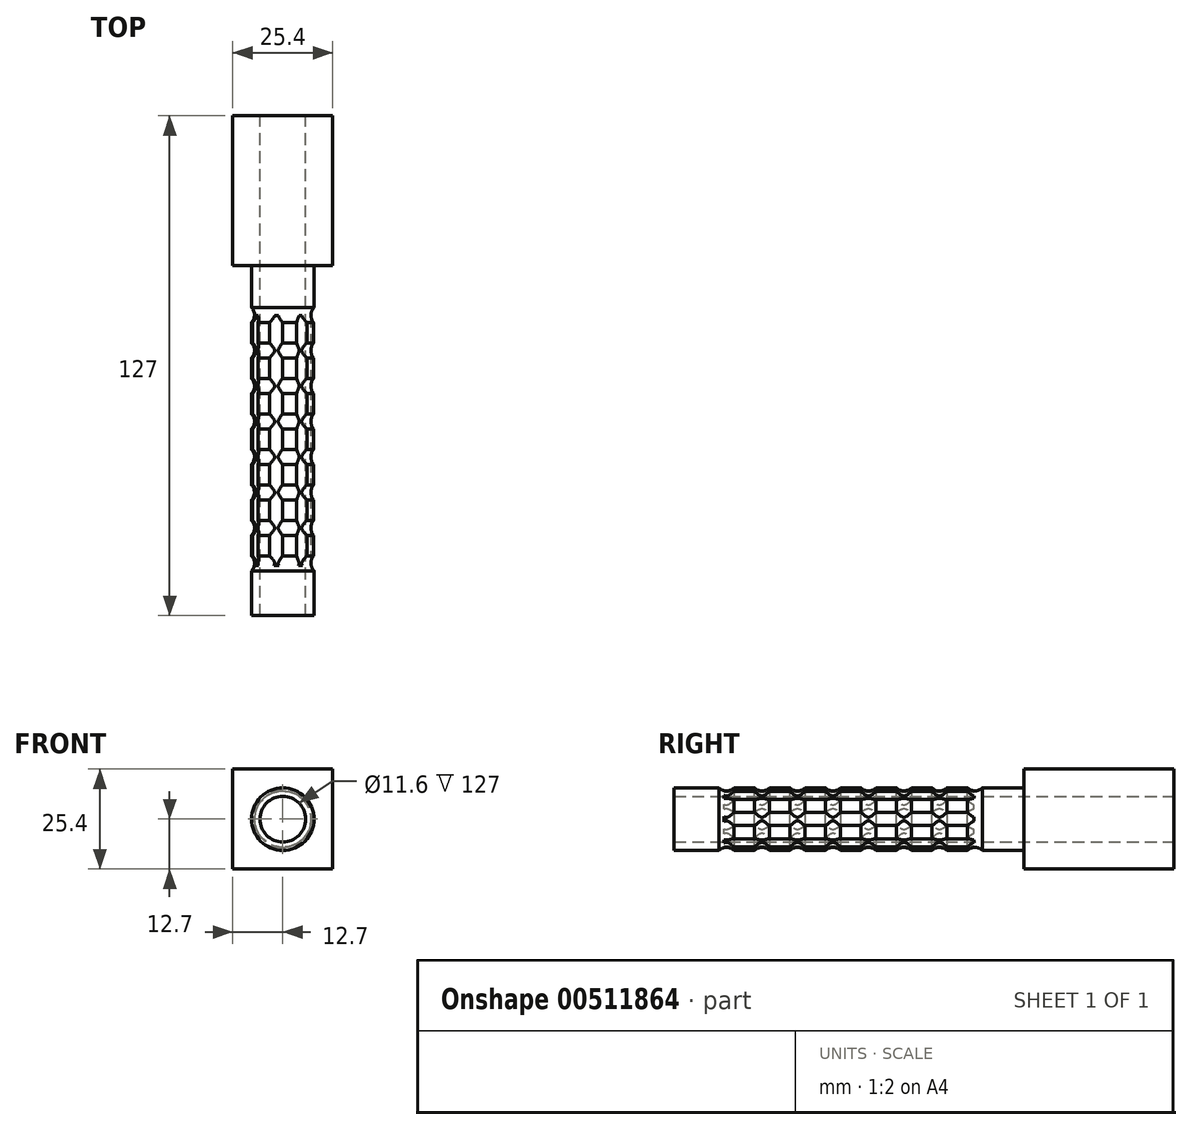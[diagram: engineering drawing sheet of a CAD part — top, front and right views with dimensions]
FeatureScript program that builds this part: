
annotation { "Feature Type Name" : "Feature", "Feature Type Description" : "" }
export const myFeature = defineFeature(function(context is Context, id is Id, definition is map)
    precondition{}
    {
        {
            var Q0;
            Q0=qCreatedBy(makeId("Front.planeOp"),FACE);
            var sketch = newSketch(context, id + "F0", { "sketchPlane" : qUnion([Q0])});
            skLineSegment(sketch, "E0.bottom", {"start": v(12.7, -12.7) * mm, "end": v(-12.7, -12.7) * mm});
            skLineSegment(sketch, "E0.top", {"start": v(12.7, 12.7) * mm, "end": v(-12.7, 12.7) * mm});
            skLineSegment(sketch, "E0.left", {"start": v(12.7, -12.7) * mm, "end": v(12.7, 12.7) * mm});
            skLineSegment(sketch, "E0.right", {"start": v(-12.7, -12.7) * mm, "end": v(-12.7, 12.7) * mm});
            skPoint(sketch, "E0.middle", {"position": v(0, 0) * mm});
            skCircle(sketch, "E1", {"center": v(0, 0) * mm, "radius": 7.94 * mm});
            skCircle(sketch, "E2", {"center": v(0, 0) * mm, "radius": 5.8 * mm});
            skSolve(sketch);
        }
        {
            var Q0;
            Q0 = qSketchRegion(id + "F0", true);
            var Q1;
            Q1=makeQuery(id+"F0.imprint","IMPRINT",FACE,{"disambiguationData":[TD([[makeQuery(id+"F0.imprint","IMPRINT",EDGE,{"derivedFrom":sQuery(id+"F0.wireOp",EDGE,"E1")}),1.0]])]});
            extrude(context, id + "F1", {"entities" : qUnion([Q0, Q1]), "depth" : 38.1 * mm});
        }
        {
            var Q0;
            Q0=makeQuery(id+"F0.imprint","IMPRINT",FACE,{"disambiguationData":[TD([[makeQuery(id+"F0.imprint","IMPRINT",EDGE,{"derivedFrom":sQuery(id+"F0.wireOp",EDGE,"E1")}),1.0]])]});
            extrude(context, id + "F2", {"entities" : qUnion([Q0]), "operationType" : NewBodyOperationType.ADD, "depth" : 127 * mm, "offsetDistance" : 25.4 * mm});
        }
        {
            var Q0;
            Q0=makeQuery(id+"F2.opExtrude","CAP_FACE",FACE,{"disambiguationData":[OSD([sQuery(id+"F0.wireOp",EDGE,"E1")])],"isStart":false});
            var sketch = newSketch(context, id + "F3", { "sketchPlane" : qUnion([Q0])});
            skCircle(sketch, "E3", {"center": v(9.58, 0) * mm, "radius": 2.46 * mm});
            skCircle(sketch, "E4.1.0", {"center": v(5.97, 7.49) * mm, "radius": 2.46 * mm});
            skCircle(sketch, "E4.2.0", {"center": v(-2.13, 9.34) * mm, "radius": 2.46 * mm});
            skCircle(sketch, "E4.3.0", {"center": v(-8.63, 4.16) * mm, "radius": 2.46 * mm});
            skCircle(sketch, "E4.4.0", {"center": v(-8.63, -4.16) * mm, "radius": 2.46 * mm});
            skCircle(sketch, "E4.5.0", {"center": v(-2.13, -9.34) * mm, "radius": 2.46 * mm});
            skCircle(sketch, "E4.6.0", {"center": v(5.97, -7.49) * mm, "radius": 2.46 * mm});
            skPoint(sketch, "E4.center", {"position": v(0, 0) * mm});
            skSolve(sketch);
        }
        {
            var Q0;
            Q0 = qSketchRegion(id + "F3", true);
            extrude(context, id + "F4", {"entities" : qUnion([Q0]), "operationType" : NewBodyOperationType.REMOVE, "oppositeDirection" : true, "depth" : 76.2 * mm, "offsetDistance" : 25.4 * mm, "hasSecondDirection" : true, "secondDirectionOppositeDirection" : true, "secondDirectionDepth" : 12.7 * mm});
        }
        {
            var Q0;
            Q0=qCreatedBy(makeId("Top.planeOp"),FACE);
            var sketch = newSketch(context, id + "F5", { "sketchPlane" : qUnion([Q0])});
            skCircle(sketch, "E5", {"center": v(-9.87, -50.6) * mm, "radius": 2.69 * mm});
            skCircle(sketch, "E6.0.1.0", {"center": v(-9.87, -59.62) * mm, "radius": 2.69 * mm});
            skCircle(sketch, "E6.0.2.0", {"center": v(-9.87, -68.64) * mm, "radius": 2.69 * mm});
            skCircle(sketch, "E6.0.3.0", {"center": v(-9.87, -77.65) * mm, "radius": 2.69 * mm});
            skCircle(sketch, "E6.0.4.0", {"center": v(-9.87, -86.67) * mm, "radius": 2.69 * mm});
            skCircle(sketch, "E6.0.5.0", {"center": v(-9.87, -95.69) * mm, "radius": 2.69 * mm});
            skCircle(sketch, "E6.0.6.0", {"center": v(-9.87, -104.7) * mm, "radius": 2.69 * mm});
            skCircle(sketch, "E6.0.7.0", {"center": v(-9.87, -113.72) * mm, "radius": 2.69 * mm});
            skLineSegment(sketch, "E6.direction1", {"start": v(-9.87, -50.6) * mm, "end": v(15.53, -50.6) * mm, "construction": true});
            skLineSegment(sketch, "E6.direction2", {"start": v(-9.87, -50.6) * mm, "end": v(-9.87, -59.62) * mm, "construction": true});
            skSolve(sketch);
        }
        {
            var Q0;
            Q0 = qSketchRegion(id + "F5", true);
            var Q1;
            {var subQ0=sQuery(id+"F0.wireOp",EDGE,"E2");Q1=makeQuery(id+"F2.boolean.opBoolean","MERGE",FACE,{"derivedFrom":[makeQuery(id+"F1.opExtrude","SWEPT_FACE",FACE,{"disambiguationData":[OSD([subQ0])]}),makeQuery(id+"F2.opExtrude","SWEPT_FACE",FACE,{"disambiguationData":[OSD([subQ0])]})]});}
            revolve(context, id + "F6", {"operationType" : NewBodyOperationType.REMOVE, "entities" : qUnion([Q0]), "axis" : qUnion([Q1]), "revolveType" : RevolveType.FULL, "oppositeDirection" : true});
        }
    });
